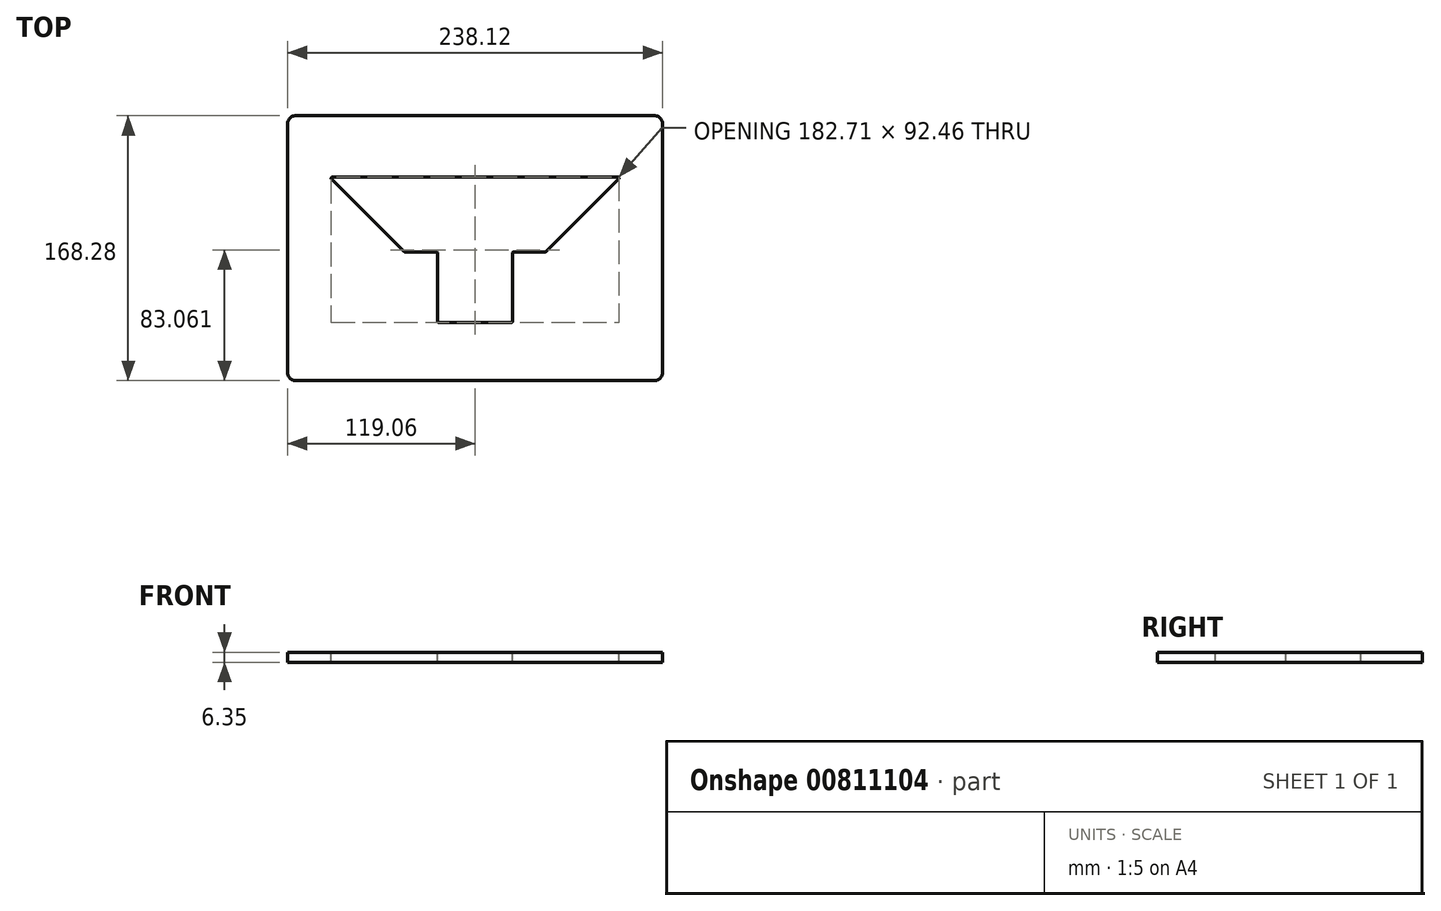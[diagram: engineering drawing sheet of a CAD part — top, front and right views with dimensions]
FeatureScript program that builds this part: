
annotation { "Feature Type Name" : "Feature", "Feature Type Description" : "" }
export const myFeature = defineFeature(function(context is Context, id is Id, definition is map)
    precondition{}
    {
        {
            var Q0;
            Q0=qCreatedBy(makeId("Top.planeOp"),FACE);
            var sketch = newSketch(context, id + "F0", { "sketchPlane" : qUnion([Q0])});
            skLineSegment(sketch, "E0.bottom", {"start": v(-113.98, 84.14) * mm, "end": v(113.98, 84.14) * mm});
            skLineSegment(sketch, "E0.top", {"start": v(-113.98, -84.14) * mm, "end": v(113.98, -84.14) * mm});
            skLineSegment(sketch, "E0.left", {"start": v(-119.06, 79.06) * mm, "end": v(-119.06, -79.06) * mm});
            skLineSegment(sketch, "E0.right", {"start": v(119.06, 79.06) * mm, "end": v(119.06, -79.06) * mm});
            skPoint(sketch, "E0.middle", {"position": v(0, 0) * mm});
            skPoint(sketch, "E1.visualSharp", {"position": v(-119.06, -84.14) * mm});
            skArc(sketch, "E1.filletArc", {"start": v(-119.06, -79.06) * mm, "mid": v(-117.57, -82.65) * mm, "end": v(-113.98, -84.14) * mm});
            skPoint(sketch, "E2.visualSharp", {"position": v(-119.06, 84.14) * mm});
            skArc(sketch, "E2.filletArc", {"start": v(-113.98, 84.14) * mm, "mid": v(-117.57, 82.65) * mm, "end": v(-119.06, 79.06) * mm});
            skPoint(sketch, "E3.visualSharp", {"position": v(119.06, -84.14) * mm});
            skArc(sketch, "E3.filletArc", {"start": v(113.98, -84.14) * mm, "mid": v(117.57, -82.65) * mm, "end": v(119.06, -79.06) * mm});
            skPoint(sketch, "E4.visualSharp", {"position": v(119.06, 84.14) * mm});
            skArc(sketch, "E4.filletArc", {"start": v(119.06, 79.06) * mm, "mid": v(117.57, 82.65) * mm, "end": v(113.98, 84.14) * mm});
            skSolve(sketch);
        }
        {
            var Q0;
            Q0 = qSketchRegion(id + "F0", true);
            extrude(context, id + "F1", {"entities" : qUnion([Q0]), "depth" : 6.35 * mm, "offsetDistance" : 25.4 * mm});
        }
        {
            var Q0;
            Q0=makeQuery(id+"F1.opExtrude","CAP_FACE",FACE,{"disambiguationData":[OSD([sQuery(id+"F0.wireOp",EDGE,"E0.bottom"),sQuery(id+"F0.wireOp",EDGE,"E0.top"),sQuery(id+"F0.wireOp",EDGE,"E0.left"),sQuery(id+"F0.wireOp",EDGE,"E0.right"),sQuery(id+"F0.wireOp",EDGE,"E1.filletArc"),sQuery(id+"F0.wireOp",EDGE,"E2.filletArc"),sQuery(id+"F0.wireOp",EDGE,"E3.filletArc"),sQuery(id+"F0.wireOp",EDGE,"E4.filletArc")])],"isStart":false});
            var sketch = newSketch(context, id + "F2", { "sketchPlane" : qUnion([Q0])});
            skLineSegment(sketch, "E5", {"start": v(0, 43.88) * mm, "end": v(-89.4, 43.88) * mm});
            skLineSegment(sketch, "E6", {"start": v(-89.4, 43.88) * mm, "end": v(-44.45, -1.08) * mm});
            skLineSegment(sketch, "E7", {"start": v(-44.45, -1.08) * mm, "end": v(-22.48, -1.08) * mm});
            skLineSegment(sketch, "E8", {"start": v(-22.48, -1.08) * mm, "end": v(-22.48, -46.04) * mm});
            skLineSegment(sketch, "E9", {"start": v(-22.48, -46.04) * mm, "end": v(0, -46.04) * mm});
            skLineSegment(sketch, "E10.MirrorCS", {"start": v(0, 43.88) * mm, "end": v(89.4, 43.88) * mm});
            skLineSegment(sketch, "E11.MirrorCS", {"start": v(89.4, 43.88) * mm, "end": v(44.45, -1.08) * mm});
            skLineSegment(sketch, "E12.MirrorCS", {"start": v(44.45, -1.08) * mm, "end": v(22.48, -1.08) * mm});
            skLineSegment(sketch, "E13.MirrorCS", {"start": v(22.48, -1.08) * mm, "end": v(22.48, -46.04) * mm});
            skLineSegment(sketch, "E14.MirrorCS", {"start": v(22.48, -46.04) * mm, "end": v(0, -46.04) * mm});
            skSolve(sketch);
        }
        {
            var Q0;
            Q0 = qSketchRegion(id + "F2", true);
            extrude(context, id + "F3", {"entities" : qUnion([Q0]), "operationType" : NewBodyOperationType.REMOVE, "oppositeDirection" : true, "depth" : 25.4 * mm, "offsetDistance" : 25.4 * mm});
        }
        {
            var Q0;
            Q0=makeQuery(id+"F1.opExtrude","CAP_FACE",FACE,{"disambiguationData":[OSD([sQuery(id+"F0.wireOp",EDGE,"E0.bottom"),sQuery(id+"F0.wireOp",EDGE,"E0.top"),sQuery(id+"F0.wireOp",EDGE,"E0.left"),sQuery(id+"F0.wireOp",EDGE,"E0.right"),sQuery(id+"F0.wireOp",EDGE,"E1.filletArc"),sQuery(id+"F0.wireOp",EDGE,"E2.filletArc"),sQuery(id+"F0.wireOp",EDGE,"E3.filletArc"),sQuery(id+"F0.wireOp",EDGE,"E4.filletArc")])],"isStart":false});
            var sketch = newSketch(context, id + "F4", { "sketchPlane" : qUnion([Q0])});
            skLineSegment(sketch, "E15.0", {"start": v(-91.13, 43.8) * mm, "end": v(-45.2, -2.12) * mm});
            skLineSegment(sketch, "E15.1", {"start": v(-44.65, -2.35) * mm, "end": v(-24.54, -2.35) * mm});
            skLineSegment(sketch, "E15.2", {"start": v(-90.57, 45.15) * mm, "end": v(90.57, 45.15) * mm});
            skLineSegment(sketch, "E15.3", {"start": v(-23.75, -3.14) * mm, "end": v(-23.75, -46.52) * mm});
            skLineSegment(sketch, "E15.4", {"start": v(91.13, 43.8) * mm, "end": v(45.2, -2.12) * mm});
            skLineSegment(sketch, "E15.5", {"start": v(44.65, -2.35) * mm, "end": v(24.54, -2.35) * mm});
            skLineSegment(sketch, "E15.6", {"start": v(23.75, -3.14) * mm, "end": v(23.75, -46.52) * mm});
            skLineSegment(sketch, "E15.7", {"start": v(22.96, -47.3) * mm, "end": v(-22.96, -47.3) * mm});
            skPoint(sketch, "E16.visualSharp", {"position": v(-92.47, 45.15) * mm});
            skArc(sketch, "E16.filletArc", {"start": v(-90.57, 45.15) * mm, "mid": v(-91.3, 44.66) * mm, "end": v(-91.13, 43.8) * mm});
            skPoint(sketch, "E17.visualSharp", {"position": v(92.47, 45.15) * mm});
            skArc(sketch, "E17.filletArc", {"start": v(91.13, 43.8) * mm, "mid": v(91.3, 44.66) * mm, "end": v(90.57, 45.15) * mm});
            skPoint(sketch, "E18.visualSharp", {"position": v(44.98, -2.35) * mm});
            skArc(sketch, "E18.filletArc", {"start": v(44.65, -2.35) * mm, "mid": v(44.95, -2.29) * mm, "end": v(45.2, -2.12) * mm});
            skPoint(sketch, "E19.visualSharp", {"position": v(23.75, -2.35) * mm});
            skArc(sketch, "E19.filletArc", {"start": v(24.54, -2.35) * mm, "mid": v(23.98, -2.58) * mm, "end": v(23.75, -3.14) * mm});
            skPoint(sketch, "E20.visualSharp", {"position": v(23.75, -47.3) * mm});
            skArc(sketch, "E20.filletArc", {"start": v(22.96, -47.3) * mm, "mid": v(23.52, -47.08) * mm, "end": v(23.75, -46.52) * mm});
            skPoint(sketch, "E21.visualSharp", {"position": v(-23.75, -47.3) * mm});
            skArc(sketch, "E21.filletArc", {"start": v(-23.75, -46.52) * mm, "mid": v(-23.52, -47.08) * mm, "end": v(-22.96, -47.3) * mm});
            skPoint(sketch, "E22.visualSharp", {"position": v(-23.75, -2.35) * mm});
            skArc(sketch, "E22.filletArc", {"start": v(-23.75, -3.14) * mm, "mid": v(-23.98, -2.58) * mm, "end": v(-24.54, -2.35) * mm});
            skPoint(sketch, "E23.visualSharp", {"position": v(-44.98, -2.35) * mm});
            skArc(sketch, "E23.filletArc", {"start": v(-45.2, -2.12) * mm, "mid": v(-44.95, -2.29) * mm, "end": v(-44.65, -2.35) * mm});
            skSolve(sketch);
        }
        {
            var Q0;
            Q0 = qSketchRegion(id + "F4", true);
            extrude(context, id + "F5", {"entities" : qUnion([Q0]), "operationType" : NewBodyOperationType.REMOVE, "oppositeDirection" : true, "depth" : 25.4 * mm, "offsetDistance" : 25.4 * mm});
        }
    });
